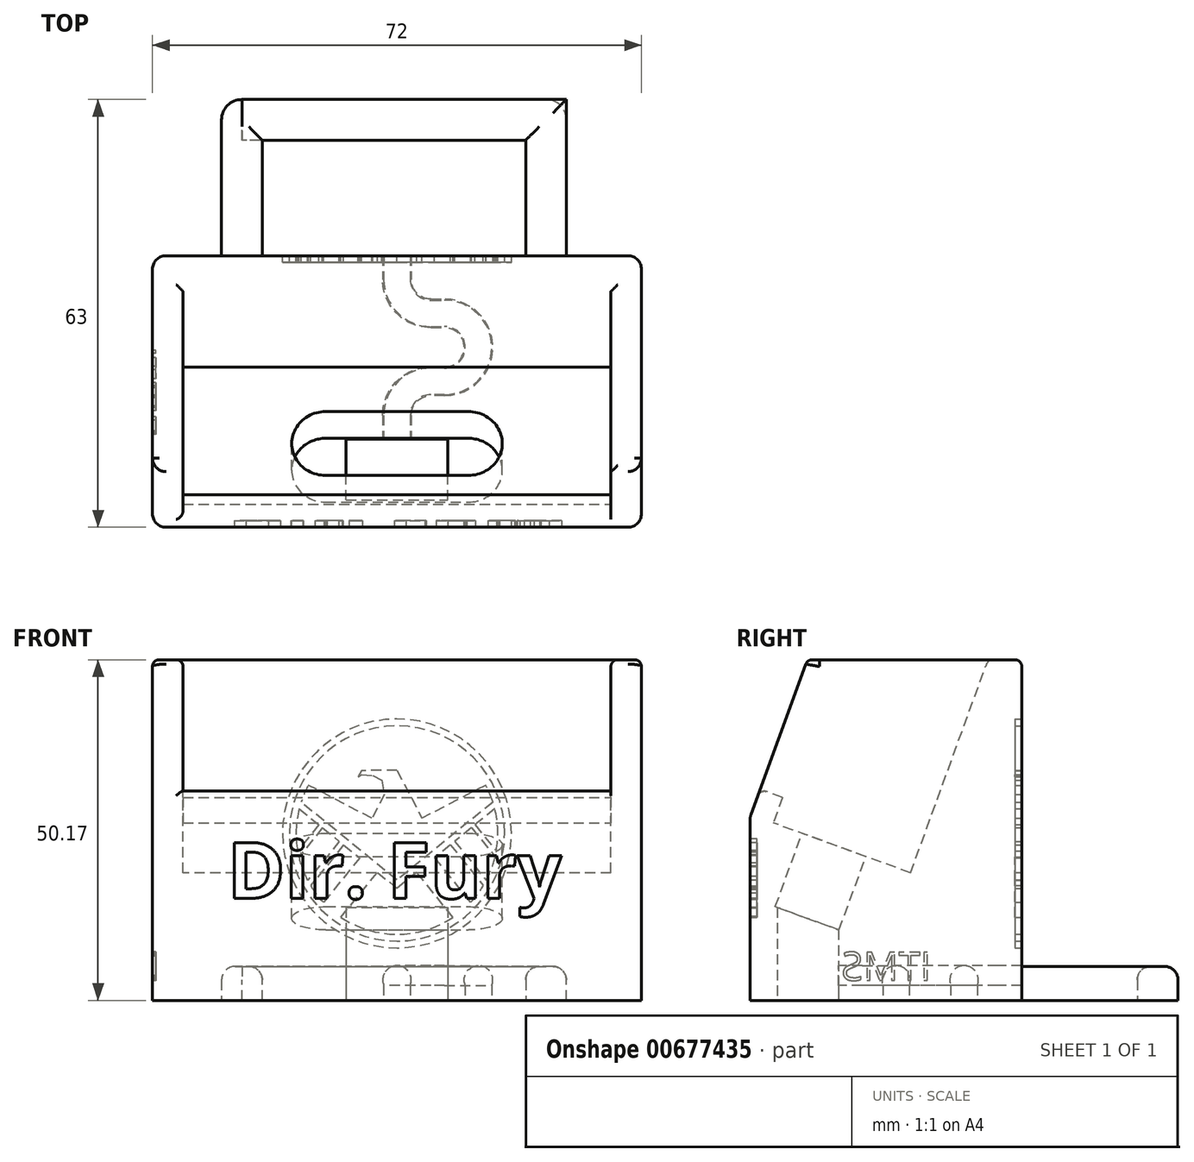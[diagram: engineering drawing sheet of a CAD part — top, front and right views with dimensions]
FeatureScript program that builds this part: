
annotation { "Feature Type Name" : "Feature", "Feature Type Description" : "" }
export const myFeature = defineFeature(function(context is Context, id is Id, definition is map)
    precondition{}
    {
        {
            var Q0;
            Q0=qCreatedBy(makeId("Right.planeOp"),FACE);
            var sketch = newSketch(context, id + "F0", { "sketchPlane" : qUnion([Q0])});
            skLineSegment(sketch, "E0", {"start": v(-9.7, -31.72) * mm, "end": v(30.3, -31.72) * mm});
            skLineSegment(sketch, "E1", {"start": v(-9.7, -31.72) * mm, "end": v(-9.7, -5.07) * mm});
            skLineSegment(sketch, "E2", {"start": v(-9.59, -4.38) * mm, "end": v(-1.28, 18.45) * mm});
            skLineSegment(sketch, "E3", {"start": v(30.3, 18.45) * mm, "end": v(30.3, -31.72) * mm});
            skPoint(sketch, "E4.visualSharp", {"position": v(-9.7, -4.72) * mm});
            skArc(sketch, "E4.filletArc", {"start": v(-9.59, -4.38) * mm, "mid": v(-9.68, -4.72) * mm, "end": v(-9.7, -5.07) * mm});
            skLineSegment(sketch, "E5", {"start": v(30.3, 18.45) * mm, "end": v(-1.28, 18.45) * mm});
            skSolve(sketch);
        }
        {
            var Q0;
            Q0=makeQuery(id+"F0.imprint","IMPRINT",FACE,{"disambiguationData":[TD([[makeQuery(id+"F0.imprint","IMPRINT",EDGE,{"derivedFrom":sQuery(id+"F0.wireOp",EDGE,"E0")}),1.0]])]});
            extrude(context, id + "F1", {"entities" : qUnion([Q0]), "depth" : 72 * mm, "offsetDistance" : 25 * mm});
        }
        {
            var Q0;
            Q0=makeQuery(id+"F1.opExtrude","SWEPT_FACE",FACE,{"disambiguationData":[OSD([sQuery(id+"F0.wireOp",EDGE,"E2"),sQuery(id+"F0.wireOp",EDGE,"K3zPJ8eX-kmVw-oXbl-nHyy-7hLOwfNmlBoX")])]});
            var sketch = newSketch(context, id + "F2", { "sketchPlane" : qUnion([Q0])});
            skLineSegment(sketch, "E6", {"start": v(4.5, -10.82) * mm, "end": v(67.5, -10.82) * mm});
            skLineSegment(sketch, "E7", {"start": v(0, 4.75) * mm, "end": v(0, 4.75) * mm});
            skLineSegment(sketch, "E8", {"start": v(72, 4.75) * mm, "end": v(72, 4.75) * mm});
            skLineSegment(sketch, "E9", {"start": v(4.5, -10.82) * mm, "end": v(4.5, 50.52) * mm});
            skLineSegment(sketch, "E10", {"start": v(67.5, -10.82) * mm, "end": v(67.5, 50.52) * mm});
            skLineSegment(sketch, "E11", {"start": v(4.5, 50.52) * mm, "end": v(67.5, 50.52) * mm});
            skLineSegment(sketch, "E12", {"start": v(0, 6.89) * mm, "end": v(4.5, 6.89) * mm, "construction": true});
            skLineSegment(sketch, "E13", {"start": v(72, 7) * mm, "end": v(67.5, 7) * mm, "construction": true});
            skSolve(sketch);
        }
        {
            var Q0;
            Q0=makeQuery(id+"F1.opExtrude","CAP_EDGE",EDGE,{"disambiguationData":[OSD([sQuery(id+"F0.wireOp",EDGE,"E2")])],"isStart":false});
            var Q1;
            Q1=makeQuery(id+"F1.opExtrude","CAP_EDGE",EDGE,{"disambiguationData":[OSD([sQuery(id+"F0.wireOp",EDGE,"E2")])],"isStart":true});
            var Q2;
            Q2=makeQuery(id+"F1.opExtrude","CAP_EDGE",EDGE,{"disambiguationData":[OSD([sQuery(id+"F0.wireOp",EDGE,"E3")])],"isStart":false});
            var Q3;
            Q3=makeQuery(id+"F1.opExtrude","CAP_EDGE",EDGE,{"disambiguationData":[OSD([sQuery(id+"F0.wireOp",EDGE,"E3")])],"isStart":true});
            fillet(context, id + "F3", {"entities" : qUnion([Q0, Q1, Q2, Q3]), "radius" : 2 * mm, "tangentPropagation" : true, "allowEdgeOverflow" : false});
        }
        {
            var Q0;
            {var subQ0=sQuery(id+"F2.wireOp",EDGE,"E11");Q0=makeQuery(id+"F2.imprint","IMPRINT",FACE,{"disambiguationData":[TD([[makeQuery(id+"F2.imprint","IMPRINT",EDGE,{"derivedFrom":subQ0}),-1.0]])]});}
            extrude(context, id + "F4", {"entities" : qUnion([Q0]), "operationType" : NewBodyOperationType.REMOVE, "oppositeDirection" : true, "depth" : 25 * mm, "offsetDistance" : 25 * mm});
        }
        {
            var Q0;
            {var subQ0=sQuery(id+"F2.wireOp",EDGE,"E9");var subQ1=sQuery(id+"F0.wireOp",EDGE,"E2");var subQ2=makeQuery(id+"F1.opExtrude","SWEPT_EDGE",EDGE,{"disambiguationData":[OSD([subQ1,sQuery(id+"F0.wireOp",EDGE,"E4.filletArc")])]});var subQ3=makeQuery(id+"F2.imprint","INTERSECT",VERTEX,{"derivedFrom":[subQ2,subQ0]});Q0=makeQuery(id+"F2.imprint","IMPRINT",FACE,{"disambiguationData":[TD([[makeQuery(id+"F2.imprint","IMPRINT",EDGE,{"disambiguationData":[TD([[subQ3,-1.0]])],"derivedFrom":subQ0}),-1.0]])]});}
            extrude(context, id + "F5", {"entities" : qUnion([Q0]), "operationType" : NewBodyOperationType.REMOVE, "oppositeDirection" : true, "depth" : 25 * mm, "offsetDistance" : 25 * mm});
        }
        {
            var Q0;
            Q0=makeQuery(id+"F5.boolean.opBoolean","COPY",FACE,{"derivedFrom":makeQuery(id+"F5.opExtrude","SWEPT_FACE",FACE,{"disambiguationData":[OSD([sQuery(id+"F0.wireOp",EDGE,"E2"),sQuery(id+"F0.wireOp",EDGE,"E4.filletArc")])]})});
            var sketch = newSketch(context, id + "F6", { "sketchPlane" : qUnion([Q0])});
            skLineSegment(sketch, "E14.bottom", {"start": v(25.5, 10.49) * mm, "end": v(46.5, 10.49) * mm});
            skLineSegment(sketch, "E14.top", {"start": v(25.5, 0.49) * mm, "end": v(46.5, 0.49) * mm});
            skLineSegment(sketch, "E14.left", {"start": v(20.5, 5.49) * mm, "end": v(20.5, 5.49) * mm});
            skLineSegment(sketch, "E14.right", {"start": v(51.5, 5.49) * mm, "end": v(51.5, 5.49) * mm});
            skPoint(sketch, "E15.visualSharp", {"position": v(20.5, 10.49) * mm});
            skArc(sketch, "E15.filletArc", {"start": v(25.5, 10.49) * mm, "mid": v(21.96, 9.02) * mm, "end": v(20.5, 5.49) * mm});
            skPoint(sketch, "E16.visualSharp", {"position": v(20.5, 0.49) * mm});
            skArc(sketch, "E16.filletArc", {"start": v(20.5, 5.49) * mm, "mid": v(21.96, 1.95) * mm, "end": v(25.5, 0.49) * mm});
            skPoint(sketch, "E17.visualSharp", {"position": v(51.5, 0.49) * mm});
            skArc(sketch, "E17.filletArc", {"start": v(46.5, 0.49) * mm, "mid": v(50.04, 1.95) * mm, "end": v(51.5, 5.49) * mm});
            skPoint(sketch, "E18.visualSharp", {"position": v(51.5, 10.49) * mm});
            skArc(sketch, "E18.filletArc", {"start": v(51.5, 5.49) * mm, "mid": v(50.04, 9.02) * mm, "end": v(46.5, 10.49) * mm});
            skLineSegment(sketch, "E19", {"start": v(20.5, 5.49) * mm, "end": v(4.5, 5.49) * mm, "construction": true});
            skPoint(sketch, "E19.endSnap0", {"position": v(4.5, 4.99) * mm});
            skLineSegment(sketch, "E20", {"start": v(51.5, 5.49) * mm, "end": v(67.5, 5.49) * mm, "construction": true});
            skLineSegment(sketch, "E21", {"start": v(4.5, -3.51) * mm, "end": v(67.5, -3.51) * mm});
            skSolve(sketch);
        }
        {
            var Q0;
            Q0=makeQuery(id+"F6.imprint","IMPRINT",FACE,{"disambiguationData":[TD([[makeQuery(id+"F6.imprint","IMPRINT",EDGE,{"derivedFrom":sQuery(id+"F6.wireOp",EDGE,"E14.bottom")}),-1.0]])]});
            extrude(context, id + "F7", {"entities" : qUnion([Q0]), "operationType" : NewBodyOperationType.REMOVE, "oppositeDirection" : true, "depth" : 11.5 * mm, "offsetDistance" : 25 * mm});
        }
        {
            var Q0;
            Q0=makeQuery(id+"F1.opExtrude","SWEPT_FACE",FACE,{"disambiguationData":[OSD([sQuery(id+"F0.wireOp",EDGE,"E0")])]});
            var sketch = newSketch(context, id + "F8", { "sketchPlane" : qUnion([Q0])});
            skLineSegment(sketch, "E22.bottom", {"start": v(28.5, 5.7) * mm, "end": v(43.5, 5.7) * mm});
            skLineSegment(sketch, "E22.top", {"start": v(28.5, -3.3) * mm, "end": v(43.5, -3.3) * mm});
            skLineSegment(sketch, "E22.left", {"start": v(28.5, 5.7) * mm, "end": v(28.5, -3.3) * mm});
            skLineSegment(sketch, "E22.right", {"start": v(43.5, 5.7) * mm, "end": v(43.5, -3.3) * mm});
            skLineSegment(sketch, "E23", {"start": v(28.5, -1.38) * mm, "end": v(0, -1.38) * mm, "construction": true});
            skLineSegment(sketch, "E24", {"start": v(43.5, -2.06) * mm, "end": v(72, -2.06) * mm, "construction": true});
            skSolve(sketch);
        }
        {
            var Q0;
            Q0=makeQuery(id+"F8.imprint","IMPRINT",FACE,{"disambiguationData":[TD([[makeQuery(id+"F8.imprint","IMPRINT",EDGE,{"derivedFrom":sQuery(id+"F8.wireOp",EDGE,"E22.bottom")}),-1.0]])]});
            extrude(context, id + "F9", {"entities" : qUnion([Q0]), "operationType" : NewBodyOperationType.REMOVE, "endBound" : BoundingType.UP_TO_NEXT, "oppositeDirection" : true, "depth" : 7 * mm, "offsetDistance" : 25 * mm});
        }
        {
            var Q0;
            Q0=makeQuery(id+"F1.opExtrude","SWEPT_FACE",FACE,{"disambiguationData":[OSD([sQuery(id+"F0.wireOp",EDGE,"E3")])]});
            var sketch = newSketch(context, id + "F10", { "sketchPlane" : qUnion([Q0])});
            skArc(sketch, "E25", {"start": v(-34.05, -29.5) * mm, "mid": v(-36, -26.62) * mm, "end": v(-37.95, -29.5) * mm});
            skLineSegment(sketch, "E26", {"start": v(-36, -28.72) * mm, "end": v(-70, -28.72) * mm, "construction": true});
            skLineSegment(sketch, "E27", {"start": v(-36, -28.72) * mm, "end": v(-2, -28.72) * mm, "construction": true});
            skLineSegment(sketch, "E28", {"start": v(-34.05, -29.5) * mm, "end": v(-34.05, -31.72) * mm});
            skLineSegment(sketch, "E29", {"start": v(-37.95, -29.5) * mm, "end": v(-37.95, -31.72) * mm});
            skSolve(sketch);
        }
        {
            var Q0;
            Q0=makeQuery(id+"F5.boolean.opBoolean","COPY",FACE,{"derivedFrom":makeQuery(id+"F5.opExtrude","SWEPT_FACE",FACE,{"disambiguationData":[OSD([sQuery(id+"F0.wireOp",EDGE,"E2"),sQuery(id+"F0.wireOp",EDGE,"E4.filletArc")])]})});
            var sketch = newSketch(context, id + "F11", { "sketchPlane" : qUnion([Q0])});
            skLineSegment(sketch, "E30", {"start": v(4.5, -4.01) * mm, "end": v(67.5, -4.01) * mm});
            skSolve(sketch);
        }
        {
            var Q0;
            {var subQ0=sQuery(id+"F11.wireOp",EDGE,"E30");Q0=makeQuery(id+"F11.imprint","IMPRINT",FACE,{"disambiguationData":[TD([[makeQuery(id+"F11.imprint","IMPRINT",EDGE,{"derivedFrom":subQ0}),-1.0]])]});}
            extrude(context, id + "F12", {"entities" : qUnion([Q0]), "operationType" : NewBodyOperationType.ADD, "depth" : 4 * mm, "offsetDistance" : 25 * mm});
        }
        {
            var Q0;
            Q0=makeQuery(id+"F1.opExtrude","CAP_EDGE",EDGE,{"disambiguationData":[OSD([sQuery(id+"F0.wireOp",EDGE,"E5")])],"isStart":true});
            var Q1;
            Q1=makeQuery(id+"F4.boolean.opBoolean","INTERSECT",EDGE,{"derivedFrom":[makeQuery(id+"F1.opExtrude","SWEPT_FACE",FACE,{"disambiguationData":[OSD([sQuery(id+"F0.wireOp",EDGE,"E5")])]}),makeQuery(id+"F4.opExtrude","SWEPT_FACE",FACE,{"disambiguationData":[OSD([sQuery(id+"F2.wireOp",EDGE,"E9")])]})]});
            var Q2;
            Q2=makeQuery(id+"F4.boolean.opBoolean","INTERSECT",EDGE,{"derivedFrom":[makeQuery(id+"F1.opExtrude","SWEPT_FACE",FACE,{"disambiguationData":[OSD([sQuery(id+"F0.wireOp",EDGE,"E5")])]}),makeQuery(id+"F4.opExtrude","SWEPT_FACE",FACE,{"disambiguationData":[OSD([sQuery(id+"F2.wireOp",EDGE,"E10")])]})]});
            var Q3;
            Q3=makeQuery(id+"F12.opExtrude","CAP_EDGE",EDGE,{"disambiguationData":[OSD([sQuery(id+"F0.wireOp",EDGE,"E2"),sQuery(id+"F0.wireOp",EDGE,"E4.filletArc")])],"isStart":false});
            var Q4;
            {var subQ0=sQuery(id+"F0.wireOp",EDGE,"E5");Q4=makeQuery(id+"F4.boolean.opBoolean","INTERSECT",EDGE,{"derivedFrom":[makeQuery(id+"F1.opExtrude","SWEPT_FACE",FACE,{"disambiguationData":[OSD([subQ0])]}),makeQuery(id+"F4.opExtrude","CAP_FACE",FACE,{"disambiguationData":[OSD([sQuery(id+"F0.wireOp",EDGE,"E2"),subQ0,sQuery(id+"F2.wireOp",EDGE,"E9"),sQuery(id+"F2.wireOp",EDGE,"E10"),sQuery(id+"F2.wireOp",EDGE,"E11")])],"isStart":false})]});}
            var Q5;
            Q5=makeQuery(id+"F5.boolean.opBoolean","COPY",EDGE,{"derivedFrom":makeQuery(id+"F5.opExtrude","CAP_EDGE",EDGE,{"disambiguationData":[OSD([sQuery(id+"F2.wireOp",EDGE,"E9")])],"isStart":true})});
            var Q6;
            Q6=makeQuery(id+"F5.boolean.opBoolean","COPY",EDGE,{"derivedFrom":makeQuery(id+"F5.opExtrude","CAP_EDGE",EDGE,{"disambiguationData":[OSD([sQuery(id+"F2.wireOp",EDGE,"E10")])],"isStart":true})});
            fillet(context, id + "F13", {"entities" : qUnion([Q0, Q1, Q2, Q3, Q4, Q5, Q6]), "radius" : 1 * mm, "tangentPropagation" : true, "defaultsChanged" : false, "vertexSettings" : [], "allowEdgeOverflow" : false});
        }
        {
            var Q0;
            Q0=makeQuery(id+"F8.imprint","IMPRINT",FACE,{"disambiguationData":[TD([[makeQuery(id+"F8.imprint","IMPRINT",EDGE,{"derivedFrom":sQuery(id+"F8.wireOp",EDGE,"E22.bottom")}),1.0]])]});
            var sketch = newSketch(context, id + "F14", { "sketchPlane" : qUnion([Q0])});
            skLineSegment(sketch, "E31", {"start": v(33.18, -30.3) * mm, "end": v(13.18, -30.3) * mm, "construction": true});
            skLineSegment(sketch, "E32", {"start": v(37.95, -30.3) * mm, "end": v(57.95, -30.3) * mm, "construction": true});
            skLineSegment(sketch, "E33", {"start": v(13.18, -30.3) * mm, "end": v(13.18, -50.3) * mm});
            skLineSegment(sketch, "E34", {"start": v(13.18, -50.3) * mm, "end": v(57.95, -50.3) * mm});
            skLineSegment(sketch, "E35", {"start": v(57.95, -50.3) * mm, "end": v(57.95, -30.3) * mm});
            skSolve(sketch);
        }
        {
            var Q0;
            Q0=makeQuery(id+"F1.opExtrude","SWEPT_FACE",FACE,{"disambiguationData":[OSD([sQuery(id+"F0.wireOp",EDGE,"E3")])]});
            var sketch = newSketch(context, id + "F15", { "sketchPlane" : qUnion([Q0])});
            skLineSegment(sketch, "E36.bottom", {"start": v(-60.95, -31.72) * mm, "end": v(-54.95, -31.72) * mm});
            skLineSegment(sketch, "E36.top", {"start": v(-58.95, -26.72) * mm, "end": v(-56.95, -26.72) * mm});
            skLineSegment(sketch, "E36.left", {"start": v(-60.95, -31.72) * mm, "end": v(-60.95, -28.72) * mm});
            skLineSegment(sketch, "E36.right", {"start": v(-54.95, -31.72) * mm, "end": v(-54.95, -28.72) * mm});
            skLineSegment(sketch, "E37.0", {"start": v(-43.5, -31.72) * mm, "end": v(-72, -31.72) * mm});
            skPoint(sketch, "E38.visualSharp", {"position": v(-60.95, -26.72) * mm});
            skArc(sketch, "E38.filletArc", {"start": v(-58.95, -26.72) * mm, "mid": v(-60.36, -27.3) * mm, "end": v(-60.95, -28.72) * mm});
            skPoint(sketch, "E39.visualSharp", {"position": v(-54.95, -26.72) * mm});
            skArc(sketch, "E39.filletArc", {"start": v(-54.95, -28.72) * mm, "mid": v(-55.54, -27.3) * mm, "end": v(-56.95, -26.72) * mm});
            skSolve(sketch);
        }
        {
            var Q0;
            Q0=makeQuery(id+"F15.imprint","IMPRINT",FACE,{"disambiguationData":[TD([[makeQuery(id+"F15.imprint","IMPRINT",EDGE,{"derivedFrom":sQuery(id+"F15.wireOp",EDGE,"E36.top")}),-1.0]])]});
            var Q1;
            Q1=sQuery(id+"F14.wireOp",EDGE,"E35");
            var Q2;
            Q2=sQuery(id+"F14.wireOp",EDGE,"E34");
            sweep(context, id + "F16", {"profiles" : qUnion([Q0]), "path" : qUnion([Q1, Q2])});
        }
        {
            var Q0;
            Q0=makeQuery(id+"F16.opSweep","CAP_FACE",FACE,{"disambiguationData":[OSD([sQuery(id+"F14.wireOp",VERTEX,"E34.start"),sQuery(id+"F15.wireOp",EDGE,"E36.top"),sQuery(id+"F15.wireOp",EDGE,"E36.left"),sQuery(id+"F15.wireOp",EDGE,"E36.right"),sQuery(id+"F15.wireOp",EDGE,"E37.0")])],"isStart":false});
            var Q1;
            Q1 = qConstructionFilter(qBodyType(qCreatedBy(id + "F14" ,EDGE), BodyType.WIRE), ConstructionObject.NO);
            sweep(context, id + "F17", {"profiles" : qUnion([Q0]), "path" : qUnion([Q1])});
        }
        {
            var Q0;
            Q0=makeQuery(id+"F17.opSweep","MID_CAP_EDGE",EDGE,{"disambiguationData":[OSD([sQuery(id+"F14.wireOp",VERTEX,"E34.start"),sQuery(id+"F14.wireOp",VERTEX,"E35.start"),sQuery(id+"F15.wireOp",EDGE,"E36.left")])],"capPos":1.0});
            var Q1;
            Q1=makeQuery(id+"F17.opSweep","MID_CAP_EDGE",EDGE,{"disambiguationData":[OSD([sQuery(id+"F14.wireOp",VERTEX,"E34.start"),sQuery(id+"F15.wireOp",EDGE,"E36.left")])],"capPos":2.0});
            fillet(context, id + "F18", {"entities" : qUnion([Q0, Q1]), "radius" : 3 * mm, "tangentPropagation" : true, "allowEdgeOverflow" : false});
        }
        {
            var Q0;
            Q0=makeQuery(id+"F1.opExtrude","SWEPT_FACE",FACE,{"disambiguationData":[OSD([sQuery(id+"F0.wireOp",EDGE,"E1")])]});
            var sketch = newSketch(context, id + "F19", { "sketchPlane" : qUnion([Q0])});
            skText(sketch, "E40", { "text": "Dir. Fury", "fontName": "OpenSans-Bold.ttf"});
            skLineSegment(sketch, "E41", {"start": v(61, -12.56) * mm, "end": v(70, -12.56) * mm, "construction": true});
            skLineSegment(sketch, "E42", {"start": v(11, -12.56) * mm, "end": v(2, -12.56) * mm, "construction": true});
            const initialGuessF19  = {"E40": [0.011, -0.01671, 1, 0, 0.0083]};
            skSetInitialGuess(sketch, initialGuessF19);
            skSolve(sketch);
        }
        {
            var Q0;
            Q0 = qSketchRegion(id + "F19", true);
            extrude(context, id + "F20", {"entities" : qUnion([Q0]), "operationType" : NewBodyOperationType.REMOVE, "oppositeDirection" : true, "depth" : 1 * mm, "offsetDistance" : 25 * mm});
        }
        {
            var Q0;
            Q0=makeQuery(id+"F14.imprint","IMPRINT",FACE,{"disambiguationData":[TD([[makeQuery(id+"F14.imprint","IMPRINT",EDGE,{"derivedFrom":makeQuery(id+"F8.imprint","IMPRINT",EDGE,{"derivedFrom":sQuery(id+"F8.wireOp",EDGE,"E22.bottom")})}),1.0]])]});
            var sketch = newSketch(context, id + "F21", { "sketchPlane" : qUnion([Q0])});
            skLineSegment(sketch, "E43", {"start": v(36, -30.3) * mm, "end": v(36, -26.8) * mm});
            skLineSegment(sketch, "E44", {"start": v(41, -21.8) * mm, "end": v(43, -21.8) * mm});
            skLineSegment(sketch, "E45", {"start": v(48, -16.8) * mm, "end": v(48, -16.8) * mm});
            skLineSegment(sketch, "E46", {"start": v(43, -11.8) * mm, "end": v(41, -11.8) * mm});
            skLineSegment(sketch, "E47", {"start": v(36, -6.8) * mm, "end": v(36, -3.3) * mm});
            skPoint(sketch, "E48.visualSharp", {"position": v(36, -21.8) * mm});
            skArc(sketch, "E48.filletArc", {"start": v(41, -21.8) * mm, "mid": v(37.46, -23.25) * mm, "end": v(36, -26.8) * mm});
            skPoint(sketch, "E49.visualSharp", {"position": v(48, -21.8) * mm});
            skArc(sketch, "E49.filletArc", {"start": v(43, -21.8) * mm, "mid": v(46.54, -20.33) * mm, "end": v(48, -16.8) * mm});
            skPoint(sketch, "E50.visualSharp", {"position": v(48, -11.8) * mm});
            skArc(sketch, "E50.filletArc", {"start": v(48, -16.8) * mm, "mid": v(46.54, -13.25) * mm, "end": v(43, -11.8) * mm});
            skPoint(sketch, "E51.visualSharp", {"position": v(36, -11.8) * mm});
            skArc(sketch, "E51.filletArc", {"start": v(36, -6.8) * mm, "mid": v(37.46, -10.33) * mm, "end": v(41, -11.8) * mm});
            skSolve(sketch);
        }
        {
            var Q0;
            Q0=makeQuery(id+"F10.imprint","IMPRINT",FACE,{"disambiguationData":[TD([[makeQuery(id+"F10.imprint","IMPRINT",EDGE,{"derivedFrom":sQuery(id+"F10.wireOp",EDGE,"E25")}),1.0]])]});
            var Q1;
            Q1 = qConstructionFilter(qBodyType(qCreatedBy(id + "F21" ,EDGE), BodyType.WIRE), ConstructionObject.NO);
            sweep(context, id + "F22", {"operationType" : NewBodyOperationType.REMOVE, "profiles" : qUnion([Q0]), "path" : qUnion([Q1])});
        }
        {
            var Q0;
            Q0=makeQuery(id+"F1.opExtrude","SWEPT_FACE",FACE,{"disambiguationData":[OSD([sQuery(id+"F0.wireOp",EDGE,"E3")])]});
            var sketch = newSketch(context, id + "F23", { "sketchPlane" : qUnion([Q0])});
            skLineSegment(sketch, "E52", {"start": v(-70, -7.13) * mm, "end": v(-2, -7.13) * mm, "construction": true});
            skLineSegment(sketch, "E53", {"start": v(-36, 17.45) * mm, "end": v(-36, -7.13) * mm, "construction": true});
            skCircle(sketch, "E54", {"center": v(-36, -7.13) * mm, "radius": 16.85 * mm});
            skCircle(sketch, "E55", {"center": v(-36, -7.13) * mm, "radius": 15.85 * mm});
            skArc(sketch, "E56", {"start": v(-49.04, -0.03) * mm, "mid": v(-49.64, -1.25) * mm, "end": v(-50.12, -2.53) * mm});
            skLineSegment(sketch, "E57", {"start": v(-36, -7.13) * mm, "end": v(-36, -29.5) * mm, "construction": true});
            skLineSegment(sketch, "E58", {"start": v(-50.12, -2.53) * mm, "end": v(-36, -14) * mm});
            skLineSegment(sketch, "E59", {"start": v(-36, -14) * mm, "end": v(-21.88, -2.53) * mm});
            skLineSegment(sketch, "E60", {"start": v(-49.04, -0.03) * mm, "end": v(-39.68, -4.9) * mm});
            skLineSegment(sketch, "E61", {"start": v(-39.68, -4.9) * mm, "end": v(-49.04, -0.03) * mm});
            skLineSegment(sketch, "E62", {"start": v(-36, 2.16) * mm, "end": v(-39.68, -4.9) * mm});
            skLineSegment(sketch, "E63.MirrorCS", {"start": v(-34.16, -1.38) * mm, "end": v(-32.32, -4.9) * mm});
            skLineSegment(sketch, "E64", {"start": v(-36, 2.16) * mm, "end": v(-30.79, 2.13) * mm});
            skLineSegment(sketch, "E65", {"start": v(-30.79, 2.13) * mm, "end": v(-30.24, 1.23) * mm});
            skLineSegment(sketch, "E66", {"start": v(-30.24, 1.23) * mm, "end": v(-30.81, 1.52) * mm});
            skPoint(sketch, "E67.1.internal.snap0", {"position": v(-33.4, 2.14) * mm});
            skLineSegment(sketch, "E68", {"start": v(-30.81, 1.52) * mm, "end": v(-32.43, 1.37) * mm});
            skPoint(sketch, "E68.endSnap0", {"position": v(-30.53, 1.37) * mm});
            skLineSegment(sketch, "E69", {"start": v(-32.43, 1.37) * mm, "end": v(-33.75, 0.67) * mm});
            skLineSegment(sketch, "E70", {"start": v(-33.75, 0.67) * mm, "end": v(-34.16, -1.38) * mm});
            skLineSegment(sketch, "E71.MirrorCS", {"start": v(-32.32, -4.9) * mm, "end": v(-22.96, -0.03) * mm});
            skPoint(sketch, "E72.orphan", {"position": v(-36, -6.82) * mm});
            skPoint(sketch, "E73.orphan", {"position": v(-36, 2.16) * mm});
            skLineSegment(sketch, "E74", {"start": v(-50.4, -3.51) * mm, "end": v(-47.5, -5.87) * mm});
            skLineSegment(sketch, "E75", {"start": v(-47.5, -5.87) * mm, "end": v(-50.63, -9.71) * mm});
            skLineSegment(sketch, "E76", {"start": v(-46.97, -6.3) * mm, "end": v(-50.45, -10.57) * mm});
            skLineSegment(sketch, "E77", {"start": v(-44.5, -8.31) * mm, "end": v(-49.15, -14.04) * mm});
            skLineSegment(sketch, "E78", {"start": v(-43.85, -8.83) * mm, "end": v(-48.71, -14.81) * mm});
            skLineSegment(sketch, "E79", {"start": v(-41.5, -10.74) * mm, "end": v(-46.83, -17.3) * mm});
            skLineSegment(sketch, "E80", {"start": v(-44.26, -19.48) * mm, "end": v(-38.89, -12.86) * mm});
            skLineSegment(sketch, "E81.trimOffspring", {"start": v(-46.97, -6.3) * mm, "end": v(-44.5, -8.31) * mm});
            skLineSegment(sketch, "E82.trimOffspring", {"start": v(-43.85, -8.83) * mm, "end": v(-41.5, -10.74) * mm});
            skLineSegment(sketch, "E83.trimOffspring", {"start": v(-38.89, -12.86) * mm, "end": v(-36, -15.2) * mm});
            skArc(sketch, "E84.trimOffspring", {"start": v(-50.4, -3.51) * mm, "mid": v(-50.84, -6.6) * mm, "end": v(-50.63, -9.71) * mm});
            skArc(sketch, "E85.trimOffspring", {"start": v(-50.45, -10.57) * mm, "mid": v(-49.9, -12.35) * mm, "end": v(-49.15, -14.04) * mm});
            skArc(sketch, "E86.trimOffspring", {"start": v(-48.71, -14.81) * mm, "mid": v(-47.84, -16.1) * mm, "end": v(-46.83, -17.3) * mm});
            skArc(sketch, "E87.trimOffspring", {"start": v(-44.26, -19.48) * mm, "mid": v(-36, -21.98) * mm, "end": v(-27.74, -19.48) * mm});
            skLineSegment(sketch, "E88.MirrorCS", {"start": v(-27.74, -19.48) * mm, "end": v(-33.11, -12.86) * mm});
            skLineSegment(sketch, "E89.MirrorCS", {"start": v(-33.11, -12.86) * mm, "end": v(-36, -15.2) * mm});
            skLineSegment(sketch, "E90.MirrorCS", {"start": v(-30.5, -10.74) * mm, "end": v(-25.17, -17.3) * mm});
            skLineSegment(sketch, "E91.MirrorCS", {"start": v(-28.15, -8.83) * mm, "end": v(-23.29, -14.81) * mm});
            skLineSegment(sketch, "E92.MirrorCS", {"start": v(-28.15, -8.83) * mm, "end": v(-30.5, -10.74) * mm});
            skArc(sketch, "E93.MirrorCS", {"start": v(-23.29, -14.81) * mm, "mid": v(-24.16, -16.1) * mm, "end": v(-25.17, -17.3) * mm});
            skArc(sketch, "E94.MirrorCS", {"start": v(-21.55, -10.57) * mm, "mid": v(-22.1, -12.35) * mm, "end": v(-22.85, -14.04) * mm});
            skLineSegment(sketch, "E95.MirrorCS", {"start": v(-25.03, -6.3) * mm, "end": v(-21.55, -10.57) * mm});
            skLineSegment(sketch, "E96.MirrorCS", {"start": v(-27.5, -8.31) * mm, "end": v(-22.85, -14.04) * mm});
            skLineSegment(sketch, "E97.MirrorCS", {"start": v(-25.03, -6.3) * mm, "end": v(-27.5, -8.31) * mm});
            skLineSegment(sketch, "E98.MirrorCS", {"start": v(-21.6, -3.51) * mm, "end": v(-24.5, -5.87) * mm});
            skArc(sketch, "E99.MirrorCS", {"start": v(-21.6, -3.51) * mm, "mid": v(-21.16, -6.6) * mm, "end": v(-21.37, -9.71) * mm});
            skLineSegment(sketch, "E100.MirrorCS", {"start": v(-24.5, -5.87) * mm, "end": v(-21.37, -9.71) * mm});
            skArc(sketch, "E101.trimOffspring", {"start": v(-21.37, -9.71) * mm, "mid": v(-21.16, -6.6) * mm, "end": v(-21.6, -3.51) * mm});
            skArc(sketch, "E102.trimOffspring", {"start": v(-22.85, -14.04) * mm, "mid": v(-22.1, -12.35) * mm, "end": v(-21.55, -10.57) * mm});
            skArc(sketch, "E103.trimOffspring", {"start": v(-25.17, -17.3) * mm, "mid": v(-24.16, -16.1) * mm, "end": v(-23.29, -14.81) * mm});
            skArc(sketch, "E104.trimOffspring", {"start": v(-21.88, -2.53) * mm, "mid": v(-22.36, -1.25) * mm, "end": v(-22.96, -0.03) * mm});
            skSolve(sketch);
        }
        {
            var Q0;
            Q0=makeQuery(id+"F23.imprint","IMPRINT",FACE,{"disambiguationData":[TD([[makeQuery(id+"F23.imprint","IMPRINT",EDGE,{"derivedFrom":sQuery(id+"F23.wireOp",EDGE,"E74")}),-1.0]])]});
            var Q1;
            Q1=makeQuery(id+"F23.imprint","IMPRINT",FACE,{"disambiguationData":[TD([[makeQuery(id+"F23.imprint","IMPRINT",EDGE,{"derivedFrom":sQuery(id+"F23.wireOp",EDGE,"E76")}),1.0]])]});
            var Q2;
            Q2=makeQuery(id+"F23.imprint","IMPRINT",FACE,{"disambiguationData":[TD([[makeQuery(id+"F23.imprint","IMPRINT",EDGE,{"derivedFrom":sQuery(id+"F23.wireOp",EDGE,"E78")}),1.0]])]});
            var Q3;
            Q3=makeQuery(id+"F23.imprint","IMPRINT",FACE,{"disambiguationData":[TD([[makeQuery(id+"F23.imprint","IMPRINT",EDGE,{"derivedFrom":sQuery(id+"F23.wireOp",EDGE,"E80")}),-1.0]])]});
            var Q4;
            Q4=makeQuery(id+"F23.imprint","IMPRINT",FACE,{"disambiguationData":[TD([[makeQuery(id+"F23.imprint","IMPRINT",EDGE,{"derivedFrom":sQuery(id+"F23.wireOp",EDGE,"E90.MirrorCS")}),1.0]])]});
            var Q5;
            Q5=makeQuery(id+"F23.imprint","IMPRINT",FACE,{"disambiguationData":[TD([[makeQuery(id+"F23.imprint","IMPRINT",EDGE,{"derivedFrom":sQuery(id+"F23.wireOp",EDGE,"E95.MirrorCS")}),-1.0]])]});
            var Q6;
            Q6=makeQuery(id+"F23.imprint","IMPRINT",FACE,{"disambiguationData":[TD([[makeQuery(id+"F23.imprint","IMPRINT",EDGE,{"derivedFrom":sQuery(id+"F23.wireOp",EDGE,"E98.MirrorCS")}),1.0]])]});
            var Q7;
            Q7=makeQuery(id+"F23.imprint","IMPRINT",FACE,{"disambiguationData":[TD([[makeQuery(id+"F23.imprint","IMPRINT",EDGE,{"derivedFrom":sQuery(id+"F23.wireOp",EDGE,"E56")}),1.0]])]});
            var Q8;
            Q8=makeQuery(id+"F23.imprint","IMPRINT",FACE,{"disambiguationData":[TD([[makeQuery(id+"F23.imprint","IMPRINT",EDGE,{"derivedFrom":sQuery(id+"F23.wireOp",EDGE,"E54")}),1.0]])]});
            extrude(context, id + "F24", {"entities" : qUnion([Q0, Q1, Q2, Q3, Q4, Q5, Q6, Q7, Q8]), "operationType" : NewBodyOperationType.REMOVE, "oppositeDirection" : true, "depth" : 1 * mm, "offsetDistance" : 25 * mm});
        }
        {
            var Q0;
            Q0=makeQuery(id+"F1.opExtrude","CAP_FACE",FACE,{"disambiguationData":[OSD([sQuery(id+"F0.wireOp",EDGE,"E0"),sQuery(id+"F0.wireOp",EDGE,"E1"),sQuery(id+"F0.wireOp",EDGE,"E2"),sQuery(id+"F0.wireOp",EDGE,"E3"),sQuery(id+"F0.wireOp",EDGE,"E4.filletArc"),sQuery(id+"F0.wireOp",EDGE,"E5")])],"isStart":true});
            var sketch = newSketch(context, id + "F25", { "sketchPlane" : qUnion([Q0])});
            skText(sketch, "E105", { "text": "ITMS", "fontName": "OpenSans-Regular.ttf"});
            skLineSegment(sketch, "E106", {"start": v(-16.95, -26.67) * mm, "end": v(-28.3, -26.67) * mm, "construction": true});
            skLineSegment(sketch, "E107", {"start": v(-3.63, -26.67) * mm, "end": v(7.7, -26.67) * mm, "construction": true});
            const initialGuessF25  = {"E105": [-0.01695, -0.02876, 1, 0, 0.00417]};
            skSetInitialGuess(sketch, initialGuessF25);
            skSolve(sketch);
        }
        {
            var Q0;
            Q0 = qSketchRegion(id + "F25", true);
            extrude(context, id + "F26", {"entities" : qUnion([Q0]), "operationType" : NewBodyOperationType.REMOVE, "oppositeDirection" : true, "depth" : 0.5 * mm, "offsetDistance" : 25 * mm});
        }
    });
